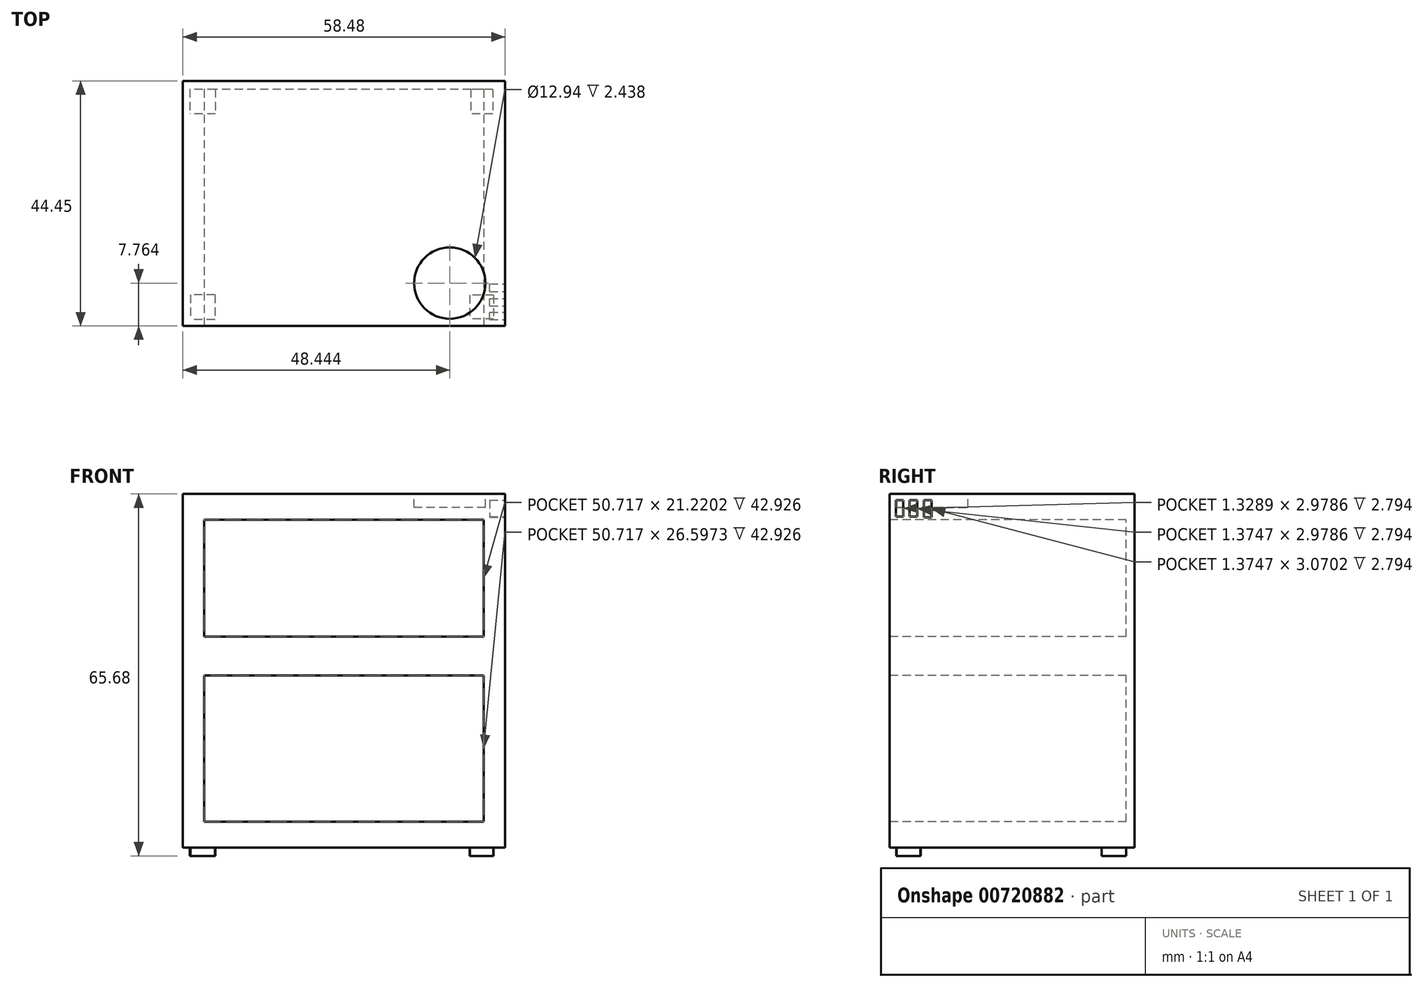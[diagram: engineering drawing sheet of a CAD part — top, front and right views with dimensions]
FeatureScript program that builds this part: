
annotation { "Feature Type Name" : "Feature", "Feature Type Description" : "" }
export const myFeature = defineFeature(function(context is Context, id is Id, definition is map)
    precondition{}
    {
        {
            var Q0;
            Q0=qCreatedBy(makeId("Front.planeOp"),FACE);
            var sketch = newSketch(context, id + "F0", { "sketchPlane" : qUnion([Q0])});
            skLineSegment(sketch, "E0.bottom", {"start": v(29.24, -32.08) * mm, "end": v(-29.24, -32.08) * mm});
            skLineSegment(sketch, "E0.top", {"start": v(29.24, 32.08) * mm, "end": v(-29.24, 32.08) * mm});
            skLineSegment(sketch, "E0.left", {"start": v(29.24, -32.08) * mm, "end": v(29.24, 32.08) * mm});
            skLineSegment(sketch, "E0.right", {"start": v(-29.24, -32.08) * mm, "end": v(-29.24, 32.08) * mm});
            skPoint(sketch, "E0.middle", {"position": v(0, 0) * mm});
            skSolve(sketch);
        }
        {
            var Q0;
            Q0=makeQuery(id+"F0.imprint","IMPRINT",FACE,{"disambiguationData":[TD([[makeQuery(id+"F0.imprint","IMPRINT",EDGE,{"derivedFrom":sQuery(id+"F0.wireOp",EDGE,"E0.bottom")}),-1.0]])]});
            extrude(context, id + "F1", {"entities" : qUnion([Q0]), "depth" : 44.45 * mm, "offsetDistance" : 25.4 * mm});
        }
        {
            var Q0;
            Q0=makeQuery(id+"F1.opExtrude","CAP_FACE",FACE,{"disambiguationData":[OSD([sQuery(id+"F0.wireOp",EDGE,"E0.bottom"),sQuery(id+"F0.wireOp",EDGE,"E0.top"),sQuery(id+"F0.wireOp",EDGE,"E0.left"),sQuery(id+"F0.wireOp",EDGE,"E0.right")])],"isStart":false});
            var sketch = newSketch(context, id + "F2", { "sketchPlane" : qUnion([Q0])});
            skLineSegment(sketch, "E1.bottom", {"start": v(25.36, 6.17) * mm, "end": v(-25.36, 6.17) * mm});
            skLineSegment(sketch, "E1.top", {"start": v(25.36, 27.4) * mm, "end": v(-25.36, 27.4) * mm});
            skLineSegment(sketch, "E1.left", {"start": v(25.36, 6.17) * mm, "end": v(25.36, 27.4) * mm});
            skLineSegment(sketch, "E1.right", {"start": v(-25.36, 6.17) * mm, "end": v(-25.36, 27.4) * mm});
            skPoint(sketch, "E1.middle", {"position": v(0, 16.78) * mm});
            skLineSegment(sketch, "E2.bottom", {"start": v(25.36, -27.42) * mm, "end": v(-25.36, -27.42) * mm});
            skLineSegment(sketch, "E2.top", {"start": v(25.36, -0.83) * mm, "end": v(-25.36, -0.83) * mm});
            skLineSegment(sketch, "E2.left", {"start": v(25.36, -27.42) * mm, "end": v(25.36, -0.83) * mm});
            skLineSegment(sketch, "E2.right", {"start": v(-25.36, -27.42) * mm, "end": v(-25.36, -0.83) * mm});
            skPoint(sketch, "E2.middle", {"position": v(0, -14.13) * mm});
            skSolve(sketch);
        }
        {
            var Q0;
            Q0=makeQuery(id+"F2.imprint","IMPRINT",FACE,{"disambiguationData":[TD([[makeQuery(id+"F2.imprint","IMPRINT",EDGE,{"derivedFrom":sQuery(id+"F2.wireOp",EDGE,"E2.bottom")}),-1.0]])]});
            var Q1;
            Q1=makeQuery(id+"F2.imprint","IMPRINT",FACE,{"disambiguationData":[TD([[makeQuery(id+"F2.imprint","IMPRINT",EDGE,{"derivedFrom":sQuery(id+"F2.wireOp",EDGE,"E1.bottom")}),-1.0]])]});
            extrude(context, id + "F3", {"entities" : qUnion([Q0, Q1]), "operationType" : NewBodyOperationType.REMOVE, "oppositeDirection" : true, "depth" : 42.93 * mm, "offsetDistance" : 25.4 * mm});
        }
        {
            var Q0;
            Q0=makeQuery(id+"F1.opExtrude","SWEPT_FACE",FACE,{"disambiguationData":[OSD([sQuery(id+"F0.wireOp",EDGE,"E0.bottom")])]});
            var sketch = newSketch(context, id + "F4", { "sketchPlane" : qUnion([Q0])});
            skLineSegment(sketch, "E3.bottom", {"start": v(-23.4, 38.81) * mm, "end": v(-27.87, 38.81) * mm});
            skLineSegment(sketch, "E3.top", {"start": v(-23.4, 43.28) * mm, "end": v(-27.87, 43.28) * mm});
            skLineSegment(sketch, "E3.left", {"start": v(-23.4, 38.81) * mm, "end": v(-23.4, 43.28) * mm});
            skLineSegment(sketch, "E3.right", {"start": v(-27.87, 38.81) * mm, "end": v(-27.87, 43.28) * mm});
            skPoint(sketch, "E3.middle", {"position": v(-25.64, 41.05) * mm});
            skLineSegment(sketch, "E4.bottom", {"start": v(27.15, 38.9) * mm, "end": v(22.84, 38.9) * mm});
            skLineSegment(sketch, "E4.top", {"start": v(27.15, 43.2) * mm, "end": v(22.84, 43.2) * mm});
            skLineSegment(sketch, "E4.left", {"start": v(27.15, 38.9) * mm, "end": v(27.15, 43.2) * mm});
            skLineSegment(sketch, "E4.right", {"start": v(22.84, 38.9) * mm, "end": v(22.84, 43.2) * mm});
            skPoint(sketch, "E4.middle", {"position": v(25, 41.05) * mm});
            skPoint(sketch, "E4.middle.positionSnap0", {"position": v(-23.4, 41.05) * mm});
            skPoint(sketch, "E4.centerSnap0", {"position": v(-23.4, 41.05) * mm});
            skLineSegment(sketch, "E5.bottom", {"start": v(27, 1.51) * mm, "end": v(23, 1.51) * mm});
            skLineSegment(sketch, "E5.top", {"start": v(27, 5.98) * mm, "end": v(23, 5.98) * mm});
            skLineSegment(sketch, "E5.left", {"start": v(27, 1.51) * mm, "end": v(27, 5.98) * mm});
            skLineSegment(sketch, "E5.right", {"start": v(23, 1.51) * mm, "end": v(23, 5.98) * mm});
            skPoint(sketch, "E5.middle", {"position": v(25, 3.75) * mm});
            skPoint(sketch, "E5.middle.positionSnap0", {"position": v(25, 38.9) * mm});
            skPoint(sketch, "E5.centerSnap0", {"position": v(25, 38.9) * mm});
            skLineSegment(sketch, "E6.bottom", {"start": v(-23.32, 1.51) * mm, "end": v(-27.95, 1.51) * mm});
            skLineSegment(sketch, "E6.top", {"start": v(-23.32, 5.98) * mm, "end": v(-27.95, 5.98) * mm});
            skLineSegment(sketch, "E6.left", {"start": v(-23.32, 1.51) * mm, "end": v(-23.32, 5.98) * mm});
            skLineSegment(sketch, "E6.right", {"start": v(-27.95, 1.51) * mm, "end": v(-27.95, 5.98) * mm});
            skPoint(sketch, "E6.middle", {"position": v(-25.64, 3.75) * mm});
            skPoint(sketch, "E6.middle.positionSnap0", {"position": v(-25.64, 38.81) * mm});
            skPoint(sketch, "E6.centerSnap0", {"position": v(-25.64, 38.81) * mm});
            skSolve(sketch);
        }
        {
            var Q0;
            Q0=makeQuery(id+"F4.imprint","IMPRINT",FACE,{"disambiguationData":[TD([[makeQuery(id+"F4.imprint","IMPRINT",EDGE,{"derivedFrom":sQuery(id+"F4.wireOp",EDGE,"E3.bottom")}),-1.0]])]});
            var Q1;
            Q1=makeQuery(id+"F4.imprint","IMPRINT",FACE,{"disambiguationData":[TD([[makeQuery(id+"F4.imprint","IMPRINT",EDGE,{"derivedFrom":sQuery(id+"F4.wireOp",EDGE,"E6.bottom")}),-1.0]])]});
            var Q2;
            Q2=makeQuery(id+"F4.imprint","IMPRINT",FACE,{"disambiguationData":[TD([[makeQuery(id+"F4.imprint","IMPRINT",EDGE,{"derivedFrom":sQuery(id+"F4.wireOp",EDGE,"E5.bottom")}),-1.0]])]});
            var Q3;
            Q3=makeQuery(id+"F4.imprint","IMPRINT",FACE,{"disambiguationData":[TD([[makeQuery(id+"F4.imprint","IMPRINT",EDGE,{"derivedFrom":sQuery(id+"F4.wireOp",EDGE,"E4.bottom")}),-1.0]])]});
            extrude(context, id + "F5", {"entities" : qUnion([Q0, Q1, Q2, Q3]), "operationType" : NewBodyOperationType.ADD, "depth" : 1.52 * mm, "offsetDistance" : 25.4 * mm});
        }
        {
            var Q0;
            Q0=makeQuery(id+"F1.opExtrude","SWEPT_FACE",FACE,{"disambiguationData":[OSD([sQuery(id+"F0.wireOp",EDGE,"E0.top")])]});
            var sketch = newSketch(context, id + "F6", { "sketchPlane" : qUnion([Q0])});
            skCircle(sketch, "E7", {"center": v(19.2, -36.69) * mm, "radius": 6.47 * mm});
            skSolve(sketch);
        }
        {
            var Q0;
            Q0=makeQuery(id+"F6.imprint","IMPRINT",FACE,{"disambiguationData":[TD([[makeQuery(id+"F6.imprint","IMPRINT",EDGE,{"derivedFrom":sQuery(id+"F6.wireOp",EDGE,"E7")}),1.0]])]});
            extrude(context, id + "F7", {"entities" : qUnion([Q0]), "operationType" : NewBodyOperationType.REMOVE, "oppositeDirection" : true, "depth" : 2.44 * mm, "offsetDistance" : 25.4 * mm});
        }
        {
            var Q0;
            Q0=makeQuery(id+"F1.opExtrude","SWEPT_FACE",FACE,{"disambiguationData":[OSD([sQuery(id+"F0.wireOp",EDGE,"E0.left")])]});
            var sketch = newSketch(context, id + "F8", { "sketchPlane" : qUnion([Q0])});
            skLineSegment(sketch, "E8.bottom", {"start": v(-43.32, 30.94) * mm, "end": v(-42, 30.94) * mm});
            skLineSegment(sketch, "E8.top", {"start": v(-43.32, 27.97) * mm, "end": v(-42, 27.97) * mm});
            skLineSegment(sketch, "E8.left", {"start": v(-43.32, 30.94) * mm, "end": v(-43.32, 27.97) * mm});
            skLineSegment(sketch, "E8.right", {"start": v(-42, 30.94) * mm, "end": v(-42, 27.97) * mm});
            skLineSegment(sketch, "E9.bottom", {"start": v(-40.85, 30.94) * mm, "end": v(-39.47, 30.94) * mm});
            skLineSegment(sketch, "E9.top", {"start": v(-40.85, 27.97) * mm, "end": v(-39.47, 27.97) * mm});
            skLineSegment(sketch, "E9.left", {"start": v(-40.85, 30.94) * mm, "end": v(-40.85, 27.97) * mm});
            skLineSegment(sketch, "E9.right", {"start": v(-39.47, 30.94) * mm, "end": v(-39.47, 27.97) * mm});
            skLineSegment(sketch, "E10.bottom", {"start": v(-38.23, 30.94) * mm, "end": v(-36.86, 30.94) * mm});
            skLineSegment(sketch, "E10.top", {"start": v(-38.23, 27.87) * mm, "end": v(-36.86, 27.87) * mm});
            skLineSegment(sketch, "E10.left", {"start": v(-38.23, 30.94) * mm, "end": v(-38.23, 27.87) * mm});
            skLineSegment(sketch, "E10.right", {"start": v(-36.86, 30.94) * mm, "end": v(-36.86, 27.87) * mm});
            skSolve(sketch);
        }
        {
            var Q0;
            Q0=makeQuery(id+"F8.imprint","IMPRINT",FACE,{"disambiguationData":[TD([[makeQuery(id+"F8.imprint","IMPRINT",EDGE,{"derivedFrom":sQuery(id+"F8.wireOp",EDGE,"E10.bottom")}),-1.0]])]});
            var Q1;
            Q1=makeQuery(id+"F8.imprint","IMPRINT",FACE,{"disambiguationData":[TD([[makeQuery(id+"F8.imprint","IMPRINT",EDGE,{"derivedFrom":sQuery(id+"F8.wireOp",EDGE,"E9.bottom")}),-1.0]])]});
            var Q2;
            Q2=makeQuery(id+"F8.imprint","IMPRINT",FACE,{"disambiguationData":[TD([[makeQuery(id+"F8.imprint","IMPRINT",EDGE,{"derivedFrom":sQuery(id+"F8.wireOp",EDGE,"E8.bottom")}),-1.0]])]});
            extrude(context, id + "F9", {"entities" : qUnion([Q0, Q1, Q2]), "operationType" : NewBodyOperationType.REMOVE, "oppositeDirection" : true, "depth" : 2.8 * mm, "offsetDistance" : 25.4 * mm});
        }
    });
